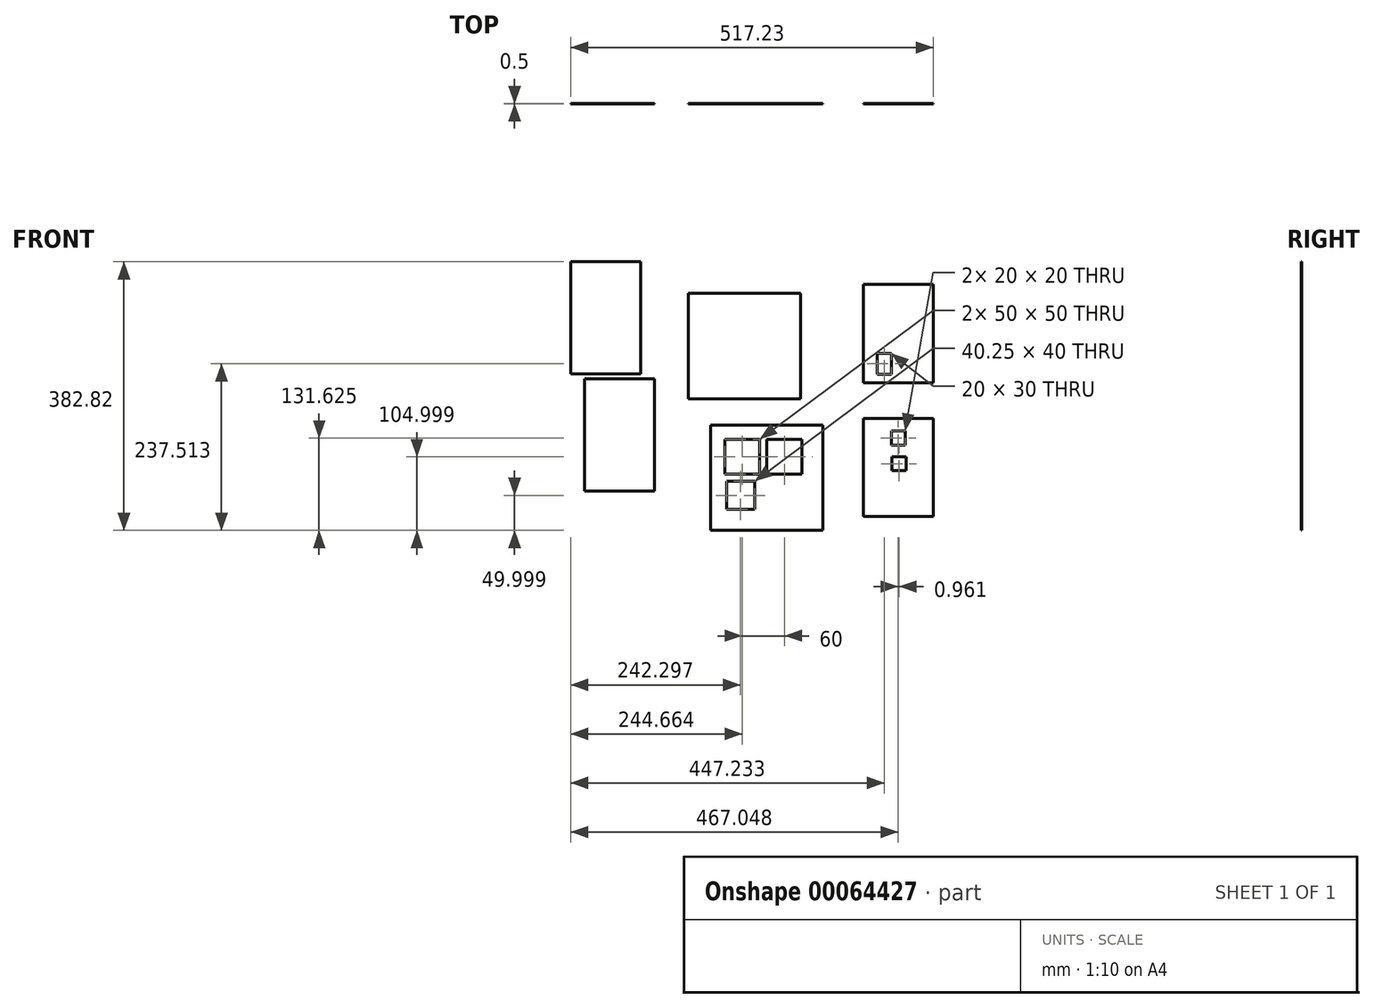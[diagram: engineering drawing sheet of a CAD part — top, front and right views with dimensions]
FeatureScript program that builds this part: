
annotation { "Feature Type Name" : "Feature", "Feature Type Description" : "" }
export const myFeature = defineFeature(function(context is Context, id is Id, definition is map)
    precondition{}
    {
        {
            var Q0;
            Q0=qCreatedBy(makeId("Front.planeOp"),FACE);
            var sketch = newSketch(context, id + "F0", { "sketchPlane" : qUnion([Q0])});
            skLineSegment(sketch, "E0.bottom", {"start": v(-135.43, -90.6) * mm, "end": v(24.57, -90.6) * mm});
            skLineSegment(sketch, "E0.top", {"start": v(-135.43, -240.6) * mm, "end": v(24.57, -240.6) * mm});
            skLineSegment(sketch, "E0.left", {"start": v(-135.43, -90.6) * mm, "end": v(-135.43, -240.6) * mm});
            skLineSegment(sketch, "E0.right", {"start": v(24.57, -90.6) * mm, "end": v(24.57, -240.6) * mm});
            skLineSegment(sketch, "E1.bottom", {"start": v(82.14, -80.78) * mm, "end": v(182.14, -80.78) * mm});
            skLineSegment(sketch, "E1.top", {"start": v(82.14, -220.78) * mm, "end": v(182.14, -220.78) * mm});
            skLineSegment(sketch, "E1.left", {"start": v(82.14, -80.78) * mm, "end": v(82.14, -220.78) * mm});
            skLineSegment(sketch, "E1.right", {"start": v(182.14, -80.78) * mm, "end": v(182.14, -220.78) * mm});
            skLineSegment(sketch, "E2.bottom", {"start": v(82.14, 110.03) * mm, "end": v(182.14, 110.03) * mm});
            skLineSegment(sketch, "E2.top", {"start": v(82.14, -29.97) * mm, "end": v(182.14, -29.97) * mm});
            skLineSegment(sketch, "E2.left", {"start": v(82.14, 110.03) * mm, "end": v(82.14, -29.97) * mm});
            skLineSegment(sketch, "E2.right", {"start": v(182.14, 110.03) * mm, "end": v(182.14, -29.97) * mm});
            skLineSegment(sketch, "E3.bottom", {"start": v(-167.07, 97.11) * mm, "end": v(-7.07, 97.11) * mm});
            skLineSegment(sketch, "E3.top", {"start": v(-167.07, -52.89) * mm, "end": v(-7.07, -52.89) * mm});
            skLineSegment(sketch, "E3.left", {"start": v(-167.07, 97.11) * mm, "end": v(-167.07, -52.89) * mm});
            skLineSegment(sketch, "E3.right", {"start": v(-7.07, 97.11) * mm, "end": v(-7.07, -52.89) * mm});
            skLineSegment(sketch, "E4.bottom", {"start": v(-335.09, 142.22) * mm, "end": v(-235.09, 142.22) * mm});
            skLineSegment(sketch, "E4.top", {"start": v(-335.09, -17.78) * mm, "end": v(-235.09, -17.78) * mm});
            skLineSegment(sketch, "E4.left", {"start": v(-335.09, 142.22) * mm, "end": v(-335.09, -17.78) * mm});
            skLineSegment(sketch, "E4.right", {"start": v(-235.09, 142.22) * mm, "end": v(-235.09, -17.78) * mm});
            skLineSegment(sketch, "E5.bottom", {"start": v(-315.39, -24.57) * mm, "end": v(-215.39, -24.57) * mm});
            skLineSegment(sketch, "E5.top", {"start": v(-315.39, -184.57) * mm, "end": v(-215.39, -184.57) * mm});
            skLineSegment(sketch, "E5.left", {"start": v(-315.39, -24.57) * mm, "end": v(-315.39, -184.57) * mm});
            skLineSegment(sketch, "E5.right", {"start": v(-215.39, -24.57) * mm, "end": v(-215.39, -184.57) * mm});
            skLineSegment(sketch, "E6.bottom", {"start": v(-115.43, -110.6) * mm, "end": v(-65.43, -110.6) * mm});
            skLineSegment(sketch, "E6.top", {"start": v(-115.43, -160.6) * mm, "end": v(-65.43, -160.6) * mm});
            skLineSegment(sketch, "E6.left", {"start": v(-115.43, -110.6) * mm, "end": v(-115.43, -160.6) * mm});
            skLineSegment(sketch, "E6.right", {"start": v(-65.43, -110.6) * mm, "end": v(-65.43, -160.6) * mm});
            skLineSegment(sketch, "E7.bottom", {"start": v(-55.43, -110.6) * mm, "end": v(-5.43, -110.6) * mm});
            skLineSegment(sketch, "E7.top", {"start": v(-55.43, -160.6) * mm, "end": v(-5.43, -160.6) * mm});
            skLineSegment(sketch, "E7.left", {"start": v(-55.43, -110.6) * mm, "end": v(-55.43, -160.6) * mm});
            skLineSegment(sketch, "E7.right", {"start": v(-5.43, -110.6) * mm, "end": v(-5.43, -160.6) * mm});
            skLineSegment(sketch, "E8.bottom", {"start": v(-112.92, -170.6) * mm, "end": v(-72.67, -170.6) * mm});
            skLineSegment(sketch, "E8.top", {"start": v(-112.92, -210.6) * mm, "end": v(-72.67, -210.6) * mm});
            skLineSegment(sketch, "E8.left", {"start": v(-112.92, -170.6) * mm, "end": v(-112.92, -210.6) * mm});
            skLineSegment(sketch, "E8.right", {"start": v(-72.67, -170.6) * mm, "end": v(-72.67, -210.6) * mm});
            skLineSegment(sketch, "E9.bottom", {"start": v(102.14, 11.91) * mm, "end": v(122.14, 11.91) * mm});
            skLineSegment(sketch, "E9.top", {"start": v(102.14, -18.09) * mm, "end": v(122.14, -18.09) * mm});
            skLineSegment(sketch, "E9.left", {"start": v(102.14, 11.91) * mm, "end": v(102.14, -18.09) * mm});
            skLineSegment(sketch, "E9.right", {"start": v(122.14, 11.91) * mm, "end": v(122.14, -18.09) * mm});
            skLineSegment(sketch, "E10.bottom", {"start": v(121.96, -98.98) * mm, "end": v(141.96, -98.98) * mm});
            skLineSegment(sketch, "E10.top", {"start": v(121.96, -118.98) * mm, "end": v(141.96, -118.98) * mm});
            skLineSegment(sketch, "E10.left", {"start": v(121.96, -98.98) * mm, "end": v(121.96, -118.98) * mm});
            skLineSegment(sketch, "E10.right", {"start": v(141.96, -98.98) * mm, "end": v(141.96, -118.98) * mm});
            skLineSegment(sketch, "E11.bottom", {"start": v(122.92, -135.49) * mm, "end": v(142.92, -135.49) * mm});
            skLineSegment(sketch, "E11.top", {"start": v(122.92, -155.49) * mm, "end": v(142.92, -155.49) * mm});
            skLineSegment(sketch, "E11.left", {"start": v(122.92, -135.49) * mm, "end": v(122.92, -155.49) * mm});
            skLineSegment(sketch, "E11.right", {"start": v(142.92, -135.49) * mm, "end": v(142.92, -155.49) * mm});
            skSolve(sketch);
        }
        {
            var Q0;
            Q0=makeQuery(id+"F0.imprint","IMPRINT",FACE,{"disambiguationData":[TD([[makeQuery(id+"F0.imprint","IMPRINT",EDGE,{"derivedFrom":sQuery(id+"F0.wireOp",EDGE,"E0.bottom")}),-1.0]])]});
            var Q1;
            Q1=makeQuery(id+"F0.imprint","IMPRINT",FACE,{"disambiguationData":[TD([[makeQuery(id+"F0.imprint","IMPRINT",EDGE,{"derivedFrom":sQuery(id+"F0.wireOp",EDGE,"E1.bottom")}),-1.0]])]});
            var Q2;
            Q2=makeQuery(id+"F0.imprint","IMPRINT",FACE,{"disambiguationData":[TD([[makeQuery(id+"F0.imprint","IMPRINT",EDGE,{"derivedFrom":sQuery(id+"F0.wireOp",EDGE,"E2.bottom")}),-1.0]])]});
            var Q3;
            Q3=makeQuery(id+"F0.imprint","IMPRINT",FACE,{"disambiguationData":[TD([[makeQuery(id+"F0.imprint","IMPRINT",EDGE,{"derivedFrom":sQuery(id+"F0.wireOp",EDGE,"E3.bottom")}),-1.0]])]});
            var Q4;
            Q4=makeQuery(id+"F0.imprint","IMPRINT",FACE,{"disambiguationData":[TD([[makeQuery(id+"F0.imprint","IMPRINT",EDGE,{"derivedFrom":sQuery(id+"F0.wireOp",EDGE,"E5.bottom")}),-1.0]])]});
            var Q5;
            Q5=makeQuery(id+"F0.imprint","IMPRINT",FACE,{"disambiguationData":[TD([[makeQuery(id+"F0.imprint","IMPRINT",EDGE,{"derivedFrom":sQuery(id+"F0.wireOp",EDGE,"E4.bottom")}),-1.0]])]});
            extrude(context, id + "F1", {"entities" : qUnion([Q0, Q1, Q2, Q3, Q4, Q5]), "depth" : 0.5 * mm});
        }
    });
